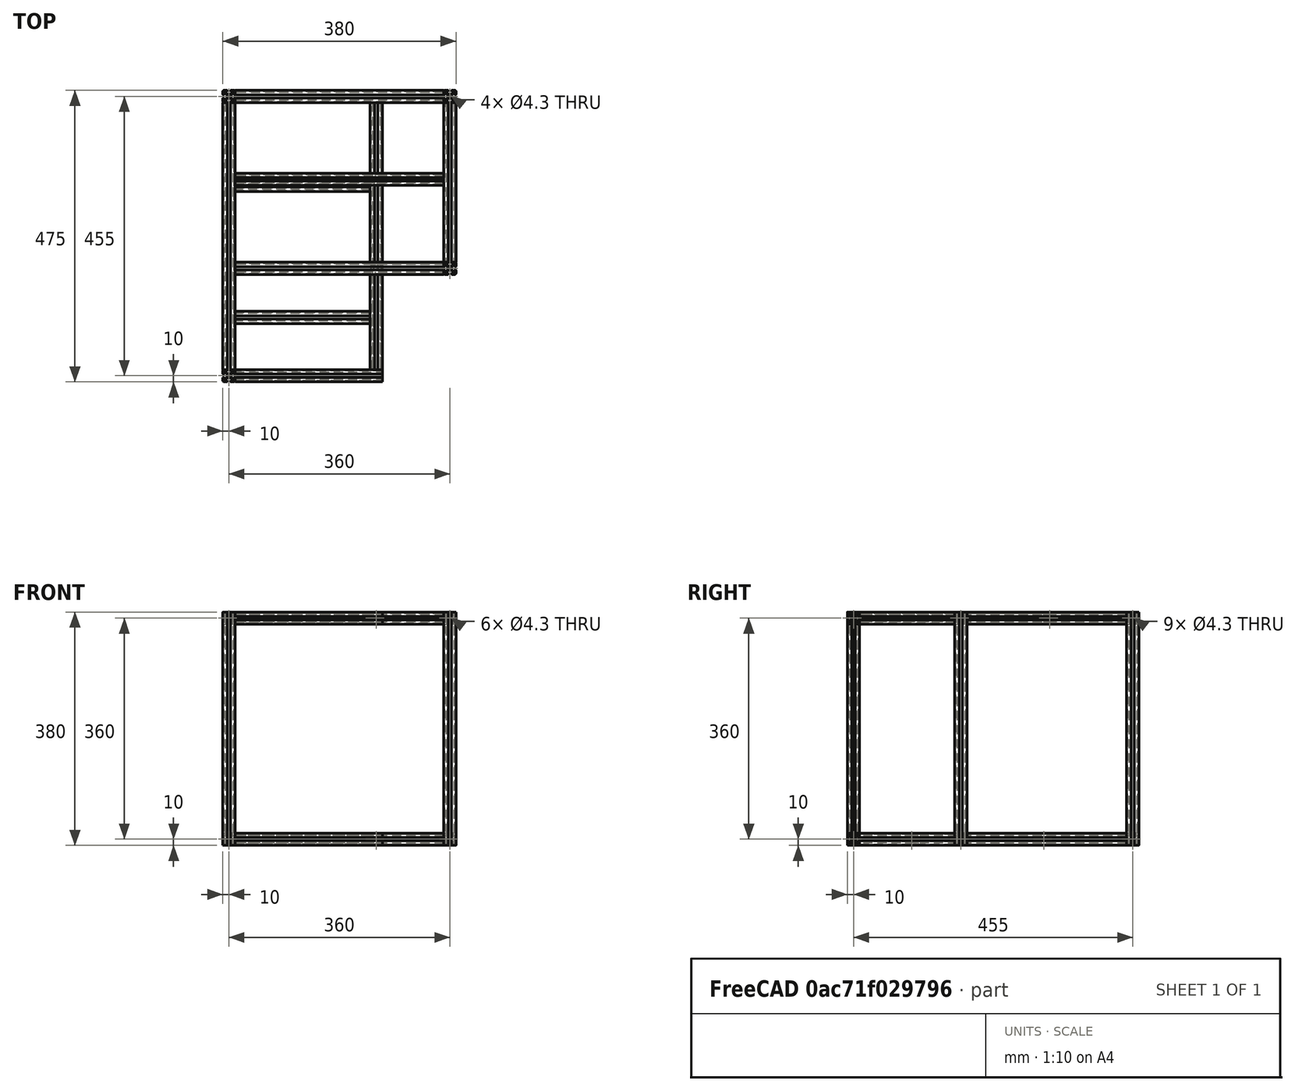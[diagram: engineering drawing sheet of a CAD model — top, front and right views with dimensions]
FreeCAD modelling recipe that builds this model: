
FCSTD DOCUMENT  (FreeCAD 0.18R)
Label: K-MINI-Enclosure-Frame
License: All rights reserved
LicenseURL: http://en.wikipedia.org/wiki/All_rights_reserved
objects: Drawing::FeatureViewPython×22, PartDesign::Pad×19, PartDesign::Body×19, Drawing::FeatureViewPart×4, Part::Compound×3, Drawing::FeaturePage×2, Sketcher::SketchObject×1, App::Part×1
note: 61 computed .brp shape members not serialized (recipe doc carries the construction recipe); baked Part::Feature solids carry a one-line shape summary decoded from their .brp

FEATURE [Sketcher::SketchObject] CopySketch029  label="ISP5-L20-Profile001"
  MapMode = 5
  sketch-geometry (70):
    g0: LineSegment StartX=-2.5 StartY=3.5 StartZ=0 EndX=-5.91967 EndY=6.91967 EndZ=0
    g1: LineSegment StartX=-5.38934 StartY=8.2 StartZ=0 EndX=-2.85 EndY=8.2 EndZ=0
    g2: LineSegment StartX=-3.35 StartY=10 StartZ=0 EndX=-8 EndY=10 EndZ=0
    g3: LineSegment StartX=-10 StartY=8 StartZ=0 EndX=-10 EndY=3.35 EndZ=0
    g4: LineSegment StartX=-9.25 StartY=2.6 StartZ=0 EndX=-8.45 EndY=2.6 EndZ=0
    g5: LineSegment StartX=-8.2 StartY=2.85 StartZ=0 EndX=-8.2 EndY=5.38934 EndZ=0
    g6: LineSegment StartX=-6.91967 StartY=5.91967 StartZ=0 EndX=-3.5 EndY=2.5 EndZ=0
    g7: LineSegment StartX=-2.6 StartY=9.25 StartZ=0 EndX=-2.6 EndY=8.45 EndZ=0
    g8: ArcOfCircle CenterX=-8 CenterY=8 CenterZ=0 NormalX=0 NormalY=0 NormalZ=1 AngleXU=0 Radius=2 StartAngle=1.5708 EndAngle=3.14159
    g9: ArcOfCircle CenterX=-3.35 CenterY=9.25 CenterZ=0 NormalX=0 NormalY=0 NormalZ=1 AngleXU=0 Radius=0.75 StartAngle=6e-16 EndAngle=1.5708
    g10: ArcOfCircle CenterX=-9.25 CenterY=3.35 CenterZ=0 NormalX=0 NormalY=0 NormalZ=1 AngleXU=0 Radius=0.75 StartAngle=3.14159 EndAngle=4.71239
    g11: ArcOfCircle CenterX=-5.38934 CenterY=7.45 CenterZ=0 NormalX=0 NormalY=0 NormalZ=1 AngleXU=0 Radius=0.75 StartAngle=1.5708 EndAngle=3.92699
    g12: ArcOfCircle CenterX=-7.45 CenterY=5.38934 CenterZ=0 NormalX=0 NormalY=0 NormalZ=1 AngleXU=0 Radius=0.75 StartAngle=0.785398 EndAngle=3.14159
    g13: LineSegment [constr] StartX=-5.38934 StartY=7.45 StartZ=0 EndX=-7.45 EndY=5.38934 EndZ=0
    g14: ArcOfCircle CenterX=-2.85 CenterY=8.45 CenterZ=0 NormalX=0 NormalY=0 NormalZ=1 AngleXU=0 Radius=0.25 StartAngle=4.71239 EndAngle=6.28319
    g15: Circle CenterX=0 CenterY=0 CenterZ=0 NormalX=0 NormalY=0 NormalZ=1 AngleXU=0 Radius=2.15
    g16: LineSegment StartX=2.5 StartY=3.5 StartZ=0 EndX=5.91967 EndY=6.91967 EndZ=0
    g17: LineSegment StartX=3.5 StartY=-2.5 StartZ=0 EndX=6.91967 EndY=-5.91967 EndZ=0
    g18: LineSegment StartX=2.5 StartY=-3.5 StartZ=0 EndX=5.91967 EndY=-6.91967 EndZ=0
    g19: LineSegment StartX=-2.5 StartY=-3.5 StartZ=0 EndX=-5.91967 EndY=-6.91967 EndZ=0
    g20: LineSegment StartX=-3.5 StartY=-2.5 StartZ=0 EndX=-6.91967 EndY=-5.91967 EndZ=0
    g21: LineSegment StartX=3.5 StartY=2.5 StartZ=0 EndX=6.91967 EndY=5.91967 EndZ=0
    g22: ArcOfCircle CenterX=-7.45 CenterY=-5.38934 CenterZ=0 NormalX=0 NormalY=0 NormalZ=1 AngleXU=0 Radius=0.75 StartAngle=3.14159 EndAngle=5.49779
    g23: ArcOfCircle CenterX=-5.38934 CenterY=-7.45 CenterZ=0 NormalX=0 NormalY=0 NormalZ=1 AngleXU=0 Radius=0.75 StartAngle=2.35619 EndAngle=4.71239
    g24: ArcOfCircle CenterX=5.38934 CenterY=-7.45 CenterZ=0 NormalX=0 NormalY=0 NormalZ=1 AngleXU=0 Radius=0.75 StartAngle=4.71239 EndAngle=7.06858
    g25: ArcOfCircle CenterX=7.45 CenterY=-5.38934 CenterZ=0 NormalX=0 NormalY=0 NormalZ=1 AngleXU=0 Radius=0.75 StartAngle=3.92699 EndAngle=6.28319
    g26: ArcOfCircle CenterX=5.38934 CenterY=7.45 CenterZ=0 NormalX=0 NormalY=0 NormalZ=1 AngleXU=0 Radius=0.75 StartAngle=5.49779 EndAngle=7.85398
    g27: ArcOfCircle CenterX=7.45 CenterY=5.38934 CenterZ=0 NormalX=0 NormalY=0 NormalZ=1 AngleXU=0 Radius=0.75 StartAngle=6e-16 EndAngle=2.35619
    g28: LineSegment StartX=-5.38934 StartY=-8.2 StartZ=0 EndX=-2.85 EndY=-8.2 EndZ=0
    g29: LineSegment StartX=2.85 StartY=-8.2 StartZ=0 EndX=5.38934 EndY=-8.2 EndZ=0
    g30: LineSegment StartX=8.2 StartY=-5.38934 StartZ=0 EndX=8.2 EndY=-2.85 EndZ=0
    g31: LineSegment StartX=8.2 StartY=5.38934 StartZ=0 EndX=8.2 EndY=2.85 EndZ=0
    g32: LineSegment StartX=5.38934 StartY=8.2 StartZ=0 EndX=2.85 EndY=8.2 EndZ=0
    g33: LineSegment StartX=-8.2 StartY=-5.38934 StartZ=0 EndX=-8.2 EndY=-2.85 EndZ=0
    g34: ArcOfCircle CenterX=-8.45 CenterY=-2.85 CenterZ=0 NormalX=0 NormalY=0 NormalZ=1 AngleXU=0 Radius=0.25 StartAngle=7e-16 EndAngle=1.5708
    g35: ArcOfCircle CenterX=-2.85 CenterY=-8.45 CenterZ=0 NormalX=0 NormalY=0 NormalZ=1 AngleXU=0 Radius=0.25 StartAngle=1e-15 EndAngle=1.5708
    g36: ArcOfCircle CenterX=2.85 CenterY=-8.45 CenterZ=0 NormalX=0 NormalY=0 NormalZ=1 AngleXU=0 Radius=0.25 StartAngle=1.5708 EndAngle=3.14159
    g37: ArcOfCircle CenterX=8.45 CenterY=-2.85 CenterZ=0 NormalX=0 NormalY=0 NormalZ=1 AngleXU=0 Radius=0.25 StartAngle=1.5708 EndAngle=3.14159
    g38: LineSegment StartX=2.6 StartY=9.25 StartZ=0 EndX=2.6 EndY=8.45 EndZ=0
    g39: LineSegment StartX=8.45 StartY=2.6 StartZ=0 EndX=9.25 EndY=2.6 EndZ=0
    g40: LineSegment StartX=8.45 StartY=-2.6 StartZ=0 EndX=9.25 EndY=-2.6 EndZ=0
    g41: LineSegment StartX=-8.45 StartY=-2.6 StartZ=0 EndX=-9.25 EndY=-2.6 EndZ=0
    g42: LineSegment StartX=-2.6 StartY=-8.45 StartZ=0 EndX=-2.6 EndY=-9.25 EndZ=0
    g43: LineSegment StartX=2.6 StartY=-8.45 StartZ=0 EndX=2.6 EndY=-9.25 EndZ=0
    g44: ArcOfCircle CenterX=8.45 CenterY=2.85 CenterZ=0 NormalX=0 NormalY=0 NormalZ=1 AngleXU=0 Radius=0.25 StartAngle=3.14159 EndAngle=4.71239
    g45: LineSegment StartX=3.35 StartY=10 StartZ=0 EndX=8 EndY=10 EndZ=0
    g46: ArcOfCircle CenterX=8 CenterY=8 CenterZ=0 NormalX=0 NormalY=0 NormalZ=1 AngleXU=0 Radius=2 StartAngle=2e-16 EndAngle=1.5708
    g47: LineSegment StartX=10 StartY=8 StartZ=0 EndX=10 EndY=3.35 EndZ=0
    g48: ArcOfCircle CenterX=9.25 CenterY=3.35 CenterZ=0 NormalX=0 NormalY=0 NormalZ=1 AngleXU=0 Radius=0.75 StartAngle=4.71239 EndAngle=6.28319
    g49: LineSegment StartX=3.35 StartY=-10 StartZ=0 EndX=8 EndY=-10 EndZ=0
    g50: ArcOfCircle CenterX=8 CenterY=-8 CenterZ=0 NormalX=0 NormalY=0 NormalZ=1 AngleXU=0 Radius=2 StartAngle=4.71239 EndAngle=6.28319
    g51: LineSegment StartX=10 StartY=-8 StartZ=0 EndX=10 EndY=-3.35 EndZ=0
    g52: ArcOfCircle CenterX=9.25 CenterY=-3.35 CenterZ=0 NormalX=0 NormalY=0 NormalZ=1 AngleXU=0 Radius=0.75 StartAngle=1e-16 EndAngle=1.5708
    g53: LineSegment StartX=-3.35 StartY=-10 StartZ=0 EndX=-8 EndY=-10 EndZ=0
    g54: LineSegment StartX=-10 StartY=-8 StartZ=0 EndX=-10 EndY=-3.35 EndZ=0
    g55: ArcOfCircle CenterX=-9.25 CenterY=-3.35 CenterZ=0 NormalX=0 NormalY=0 NormalZ=1 AngleXU=0 Radius=0.75 StartAngle=1.5708 EndAngle=3.14159
    g56: ArcOfCircle CenterX=-3.35 CenterY=-9.25 CenterZ=0 NormalX=0 NormalY=0 NormalZ=1 AngleXU=0 Radius=0.75 StartAngle=4.71239 EndAngle=6.28319
    g57: ArcOfCircle CenterX=3.35 CenterY=-9.25 CenterZ=0 NormalX=0 NormalY=0 NormalZ=1 AngleXU=0 Radius=0.75 StartAngle=3.14159 EndAngle=4.71239
    g58: ArcOfCircle CenterX=3.35 CenterY=9.25 CenterZ=0 NormalX=0 NormalY=0 NormalZ=1 AngleXU=0 Radius=0.75 StartAngle=1.5708 EndAngle=3.14159
    g59: ArcOfCircle CenterX=-8 CenterY=-8 CenterZ=0 NormalX=0 NormalY=0 NormalZ=1 AngleXU=0 Radius=2 StartAngle=3.14159 EndAngle=4.71239
    g60: ArcOfCircle CenterX=-8.45 CenterY=2.85 CenterZ=0 NormalX=0 NormalY=0 NormalZ=1 AngleXU=0 Radius=0.25 StartAngle=4.71239 EndAngle=6.28319
    g61: ArcOfCircle CenterX=2.85 CenterY=8.45 CenterZ=0 NormalX=0 NormalY=0 NormalZ=1 AngleXU=0 Radius=0.25 StartAngle=3.14159 EndAngle=4.71239
    g62: LineSegment StartX=0 StartY=3.5 StartZ=0 EndX=2.5 EndY=3.5 EndZ=0
    g63: LineSegment StartX=0 StartY=3.5 StartZ=0 EndX=-2.5 EndY=3.5 EndZ=0
    g64: LineSegment StartX=-3.5 StartY=2.5 StartZ=0 EndX=-3.5 EndY=0 EndZ=0
    g65: LineSegment StartX=-3.5 StartY=0 StartZ=0 EndX=-3.5 EndY=-2.5 EndZ=0
    g66: LineSegment StartX=-2.5 StartY=-3.5 StartZ=0 EndX=0 EndY=-3.5 EndZ=0
    g67: LineSegment StartX=0 StartY=-3.5 StartZ=0 EndX=2.5 EndY=-3.5 EndZ=0
    g68: LineSegment StartX=3.5 StartY=-2.5 StartZ=0 EndX=3.5 EndY=0 EndZ=0
    g69: LineSegment StartX=3.5 StartY=0 StartZ=0 EndX=3.5 EndY=2.5 EndZ=0
  constraints (173):
    c: Vertical(g7)
    c: Horizontal(g1)
    c: Vertical(g5)
    c: Horizontal(g4)
    c: Coincident(g2,g9)
    c: Coincident(g9,g7)
    c: Radius(g9) = 0.75
    c: DistanceY(g1,g2) = 1.8
    c: Coincident(g3,g10)
    c: Coincident(g10,g4)
    c: Radius(g10) = 0.75
    c: Horizontal(g9,g7)
    c: Vertical(g2,g9)
    c: Coincident(g0,g11)
    c: Coincident(g11,g1)
    c: Vertical(g1,g11)
    c: Radius(g11) = 0.75
    c: Coincident(g12,g6)
    c: Coincident(g12,g5)
    c: Equal(g11,g12)
    c: Horizontal(g5,g12)
    c: Coincident(g12,g13)
    c: Coincident(g11,g13)
    c: PointOnObject(g0,g13)
    c: PointOnObject(g6,g13)
    c: Horizontal(g3,g10)
    c: Vertical(g10,g4)
    c: Horizontal(g2)
    c: Vertical(g3)
    c: Parallel(g6,g0)
    c: Tangent(g2,g8) = -1.5708
    c: Tangent(g3,g8) = -1.5708
    c: Radius(g8) = 2
    c: Perpendicular(g13,g6)
    c: Coincident(g7,g14)
    c: Coincident(g1,g14)
    c: Vertical(g14,g1)
    c: Horizontal(g14,g7)
    c: Radius(g14) = 0.25
    c: DistanceX(g3,g5) = 1.8
    c: Coincident(g15,g-1)
    c: Radius(g15) = 2.15
    c: DistanceX(g0,g16) = 5
    c: Symmetric(g16,g0,g-2)
    c: Symmetric(g21,g6,g-2)
    c: Equal(g16,g21)
    c: Parallel(g20,g19)
    c: Parallel(g18,g17)
    c: Symmetric(g6,g20,g-1)
    c: Symmetric(g0,g19,g-1)
    c: Tangent(g16,g26) = -1.5708
    c: Tangent(g21,g27) = 1.5708
    c: Tangent(g17,g25) = -1.5708
    c: Tangent(g18,g24) = 1.5708
    c: Tangent(g19,g23) = -1.5708
    c: Tangent(g20,g22) = 1.5708
    c: Horizontal(g28)
    c: Tangent(g26,g32) = -1.5708
    c: Tangent(g27,g31) = 1.5708
    c: Tangent(g25,g30) = -1.5708
    c: Tangent(g24,g29) = -1.5708
    c: Tangent(g23,g28) = -1.5708
    c: Tangent(g22,g33) = 1.5708
    c: Tangent(g30,g37) = 1.5708
    c: Tangent(g36,g29) = 1.5708
    c: Tangent(g28,g35) = 1.5708
    c: Tangent(g34,g33) = -1.5708
    c: Symmetric(g0,g16,g-2)
    c: Symmetric(g21,g17,g-1)
    c: Symmetric(g18,g19,g-2)
    c: Symmetric(g6,g20,g-1)
    c: Symmetric(g23,g1,g-1)
    c: Symmetric(g24,g26,g-1)
    c: DistanceX(g6,g21) = 7
    c: Vertical(g42)
    c: Vertical(g43)
    c: Tangent(g44,g31) = -1.5708
    c: Tangent(g44,g39) = -1.5708
    c: Tangent(g37,g40) = 1.5708
    c: Tangent(g36,g43) = -1.5708
    c: Tangent(g35,g42) = 1.5708
    c: Tangent(g41,g34) = -1.5708
    c: Symmetric(g5,g27,g-2)
    c: Symmetric(g22,g25,g-2)
    c: Vertical(g7,g35)
    c: Symmetric(g4,g41,g-1)
    c: Symmetric(g7,g38,g-2)
    c: Symmetric(g39,g40,g-1)
    c: Tangent(g45,g46) = 1.5708
    c: Tangent(g46,g47) = 1.5708
    c: Tangent(g47,g48) = 1.5708
    c: Tangent(g49,g50) = -1.5708
    c: Tangent(g50,g51) = -1.5708
    c: Tangent(g51,g52) = -1.5708
    c: Tangent(g54,g55) = 1.5708
    c: Tangent(g55,g41) = -1.5708
    c: Tangent(g40,g52) = 1.5708
    c: Tangent(g48,g39) = -1.5708
    c: Vertical(g51)
    c: Vertical(g47)
    c: Horizontal(g45)
    c: Horizontal(g49)
    c: Horizontal(g53)
    c: Tangent(g45,g58) = 1.5708
    c: Tangent(g38,g58) = -1.5708
    c: Tangent(g43,g57) = -1.5708
    c: Tangent(g49,g57) = -1.5708
    c: Tangent(g53,g56) = 1.5708
    c: Tangent(g42,g56) = 1.5708
    c: DistanceX(g3,g46) = 20
    c: Tangent(g54,g59) = 1.5708
    c: Tangent(g53,g59) = 1.5708
    c: DistanceY(g53,g2) = 20
    c: Symmetric(g54,g51,g-2)
    c: Vertical(g51,g47)
    c: Horizontal(g39)
    c: Horizontal(g40)
    c: Vertical(g54)
    c: DistanceX(g7,g38) = 5.2
    c: DistanceY(g41,g4) = 5.2
    c: DistanceY(g40,g39) = 5.2
    c: Horizontal(g2,g45)
    c: Vertical(g3,g54)
    c: Horizontal(g53,g49)
    c: Vertical(g38)
    c: Horizontal(g32)
    c: Vertical(g30)
    c: Vertical(g31)
    c: Vertical(g33)
    c: Vertical(g5,g33)
    c: Horizontal(g41)
    c: Radius(g46) = 2
    c: Radius(g50) = 2
    c: Radius(g59) = 2
    c: Radius(g56) = 0.75
    c: Symmetric(g42,g43,g-2)
    c: Radius(g35) = 0.25
    c: Radius(g44) = 0.25
    c: Radius(g34) = 0.25
    c: Radius(g37) = 0.25
    c: Tangent(g5,g60) = -1.5708
    c: Tangent(g4,g60) = -1.5708
    c: Radius(g60) = 0.25
    c: Tangent(g61,g38) = -1.5708
    c: Tangent(g32,g61) = 1.5708
    c: Radius(g61) = 0.25
    c: Radius(g36) = 0.25
    c: Horizontal(g1,g32)
    c: Coincident(g62,g63)
    c: Horizontal(g63)
    c: PointOnObject(g62,g-2)
    c: Coincident(g16,g62)
    c: Coincident(g0,g63)
    c: Coincident(g68,g69)
    c: Coincident(g66,g67)
    c: Coincident(g64,g65)
    c: Coincident(g20,g65)
    c: Coincident(g19,g66)
    c: Coincident(g18,g67)
    c: Coincident(g17,g68)
    c: Coincident(g21,g69)
    c: Coincident(g6,g64)
    c: PointOnObject(g64,g-1)
    c: PointOnObject(g68,g-1)
    c: PointOnObject(g66,g-2)
    c: Vertical(g64)
    c: Horizontal(g66)
    c: Horizontal(g67)
    c: Vertical(g69)
    c: Vertical(g68)
    c: DistanceY(g20,g6) = 5
    c: DistanceY(g19,g0) = 7
    c: Vertical(g16,g18)
FEATURE [PartDesign::Pad] Pad
  Length = 380
  Length2 = 0
  Profile = -> CopySketch029
  Type = 0
FEATURE [PartDesign::Body] Body003  label="V-Front-Left"
  Group = -> [Pad]
  Origin = -> Origin008
  Placement = pos=(-215,-240,-50) rot=(0,0,1;0rad)
  Tip = -> Pad
FEATURE [PartDesign::Pad] Pad002
  Length = 380
  Length2 = 0
  Profile = -> CopySketch029
  Type = 0
FEATURE [PartDesign::Body] Body004  label="V-Back-Left"
  Group = -> [Pad002]
  Origin = -> Origin009
  Placement = pos=(-215,215,-50) rot=(0,0,1;0rad)
  Tip = -> Pad002
FEATURE [PartDesign::Pad] Pad003
  Length = 100
  Length2 = 0
  Profile = -> CopySketch029
  Type = 0
FEATURE [PartDesign::Body] Body005  label="B-X-Right"
  Group = -> [Pad003]
  Origin = -> Origin010
  Placement = pos=(35,-65,-40) rot=(0,1,0;1.5708rad)
  Tip = -> Pad003
FEATURE [PartDesign::Pad] Pad004
  Length = 380
  Length2 = 0
  Profile = -> CopySketch029
  Type = 0
FEATURE [PartDesign::Body] Body006  label="V-Back-Right"
  Group = -> [Pad004]
  Origin = -> Origin011
  Placement = pos=(145,215,-50) rot=(0,0,1;0rad)
  Tip = -> Pad004
FEATURE [PartDesign::Pad] Pad008
  Length = 220
  Length2 = 0
  Profile = -> CopySketch029
  Type = 0
FEATURE [PartDesign::Body] Body010  label="B-Carrier-Back"
  Group = -> [Pad008]
  Origin = -> Origin015
  Placement = pos=(-205,70,-40) rot=(0,1,0;1.5708rad)
  Tip = -> Pad008
FEATURE [PartDesign::Pad] Pad009
  Length = 340
  Length2 = 0
  Profile = -> CopySketch029
  Type = 0
FEATURE [PartDesign::Body] Body011  label="T-X-Back"
  Group = -> [Pad009]
  Origin = -> Origin016
  Placement = pos=(-205,215,320) rot=(0,1,0;1.5708rad)
  Tip = -> Pad009
FEATURE [PartDesign::Pad] Pad010
  Length = 240
  Length2 = 0
  Profile = -> CopySketch029
  Type = 0
FEATURE [PartDesign::Body] Body012  label="T-X-Front"
  Group = -> [Pad010]
  Origin = -> Origin017
  Placement = pos=(35,-240,320) rot=(0.707107,0,-0.707107;3.14159rad)
  Tip = -> Pad010
FEATURE [PartDesign::Pad] Pad011
  Length = 220
  Length2 = 0
  Profile = -> CopySketch029
  Type = 0
FEATURE [PartDesign::Body] Body013  label="B-Carrier-Front"
  Group = -> [Pad011]
  Origin = -> Origin018
  Placement = pos=(-205,-145,-40) rot=(0,1,0;1.5708rad)
  Tip = -> Pad011
FEATURE [PartDesign::Pad] Pad012
  Length = 435
  Length2 = 0
  Profile = -> CopySketch029
  Type = 0
FEATURE [PartDesign::Body] Body014  label="B-Y-Left"
  Group = -> [Pad012]
  Origin = -> Origin019
  Placement = pos=(-215,-230,-40) rot=(0.57735,-0.57735,-0.57735;4.18879rad)
  Tip = -> Pad012
FEATURE [PartDesign::Pad] Pad013
  Length = 260
  Length2 = 0
  Profile = -> CopySketch029
  Type = 0
FEATURE [PartDesign::Body] Body015  label="B-Y-Right"
  Group = -> [Pad013]
  Origin = -> Origin020
  Placement = pos=(145,-55,-40) rot=(0.57735,-0.57735,-0.57735;4.18879rad)
  Tip = -> Pad013
FEATURE [PartDesign::Pad] Pad014
  Length = 340
  Length2 = 0
  Profile = -> CopySketch029
  Type = 0
FEATURE [PartDesign::Body] Body016  label="T-X-Middle"
  Group = -> [Pad014]
  Origin = -> Origin021
  Placement = pos=(-205,-65,320) rot=(0,1,0;1.5708rad)
  Tip = -> Pad014
FEATURE [PartDesign::Pad] Pad015
  Length = 435
  Length2 = 0
  Profile = -> CopySketch029
  Type = 0
FEATURE [PartDesign::Body] Body017  label="T-Y-Left"
  Group = -> [Pad015]
  Origin = -> Origin022
  Placement = pos=(-215,-230,320) rot=(0.57735,-0.57735,-0.57735;4.18879rad)
  Tip = -> Pad015
FEATURE [PartDesign::Pad] Pad016
  Length = 240
  Length2 = 0
  Profile = -> CopySketch029
  Type = 0
FEATURE [PartDesign::Body] Body019  label="B-X-Front"
  Group = -> [Pad016]
  Origin = -> Origin024
  Placement = pos=(35,-240,-40) rot=(0.707107,0,-0.707107;3.14159rad)
  Tip = -> Pad016
FEATURE [PartDesign::Pad] Pad017
  Length = 340
  Length2 = 0
  Profile = -> CopySketch029
  Type = 0
FEATURE [PartDesign::Body] Body020  label="B-X-Back"
  Group = -> [Pad017]
  Origin = -> Origin025
  Placement = pos=(-205,215,-40) rot=(0,1,0;1.5708rad)
  Tip = -> Pad017
FEATURE [PartDesign::Pad] Pad018
  Length = 380
  Length2 = 0
  Profile = -> CopySketch029
  Type = 0
FEATURE [PartDesign::Body] Body021  label="V-Front-Right"
  Group = -> [Pad018]
  Origin = -> Origin026
  Placement = pos=(145,-65,-50) rot=(0,0,1;0rad)
  Tip = -> Pad018
FEATURE [Part::Compound] Compound  label="Vertical"
  Links = -> [Body003,Body004,Body006,Body021]
FEATURE [PartDesign::Pad] Pad019
  Length = 260
  Length2 = 0
  Profile = -> CopySketch029
  Type = 0
FEATURE [PartDesign::Body] Body022  label="T-Y-Right"
  Group = -> [Pad019]
  Origin = -> Origin027
  Placement = pos=(145,-55,320) rot=(0.57735,-0.57735,-0.57735;4.18879rad)
  Tip = -> Pad019
FEATURE [PartDesign::Pad] Pad024
  Length = 435
  Length2 = 0
  Profile = -> CopySketch029
  Type = 0
FEATURE [PartDesign::Body] Body027  label="B-Y-Mid"
  Group = -> [CopySketch029,Pad024]
  Origin = -> Origin032
  Placement = pos=(25,-230,-40) rot=(-1,0,0;1.5708rad)
  Tip = -> Pad024
FEATURE [Part::Compound] Compound001  label="Bottom"
  Links = -> [Body013,Body010,Body014,Body015,Body019,Body020,Body027,Body005]
FEATURE [PartDesign::Pad] Pad025
  Length = 155
  Length2 = 0
  Profile = -> CopySketch029
  Type = 0
FEATURE [PartDesign::Body] Body028  label="T-Y-Mid"
  Group = -> [Pad025]
  Origin = -> Origin033
  Placement = pos=(25,-230,320) rot=(-1,0,0;1.5708rad)
  Tip = -> Pad025
FEATURE [PartDesign::Pad] Pad026
  Length = 340
  Length2 = 100
  Profile = -> CopySketch029
  Type = 0
FEATURE [PartDesign::Body] Body029  label="T-X-HandleRear"
  Group = -> [Pad026]
  Origin = -> Origin034
  Placement = pos=(-205,80,320) rot=(0,1,0;1.5708rad)
  Tip = -> Pad026
FEATURE [Part::Compound] Compound002  label="Top"
  Links = -> [Body011,Body012,Body016,Body017,Body022,Body028,Body029]
FEATURE [App::Part] Part002  label="K-MINI-Enclosure-Frame"
  Group = -> [Body003,Body004,Body005,Body006,Compound,Body010,Body013,Compound001,Body011,Body012,Body016,Body017,Compound002]
  Origin = -> Origin004
FEATURE [Drawing::FeatureViewPart] View
  Direction = (0,0,1)
  HiddenWidth = 0.15
  LineWidth = 0.35
  Rotation = 0
  Scale = 0.25
  ShowHiddenLines = false
  ShowSmoothLines = false
  Source = -> Compound
  Tolerance = 0.05
  ViewResult = <blob: 15307 chars omitted>
  Visible = false
  X = 113.75
  Y = 145.375
FEATURE [Drawing::FeatureViewPart] View001
  Direction = (0,0,1)
  HiddenWidth = 0.15
  LineWidth = 0.35
  Rotation = 0
  Scale = 0.25
  ShowHiddenLines = false
  ShowSmoothLines = false
  Source = -> Compound002
  Tolerance = 0.05
  ViewResult = <blob: 27314 chars omitted>
  Visible = false
  X = 113.75
  Y = 145.375
FEATURE [Drawing::FeatureViewPython] centerLines001  # drawing view (typed FeaturePython)
  Rotation = 0
  ViewResult = <g transform="scale(0.250000,0.250000)" stroke="rgb(0,0,255)"  stroke-width="1.280000" > <path d="M 250.000000,646.500000 L 244.000000,646.500000 M 236.000000,646.500000 L 219.817495,646.500000 "/>\n<path d="M 250.000000,646.500000 L 244.000000,646.500000 M 236.000000,646.500000 L 219.817495,646.500000 "/> </g> 
  Visible = false
  X = 0
  Y = 0
  centerLine_color = rgb(0,0,255)
  centerLine_len_dash = 6
  centerLine_len_dot = 1.5
  centerLine_len_gap = 2
  centerLine_width = 0.32
  click1_x = 54.9544
  click1_y = 162.545
  click2_x = 54.9544
  click2_y = 161.848
FEATURE [Drawing::FeatureViewPython] centerLines002  # drawing view (typed FeaturePython)
  Rotation = 0
  ViewResult = <g transform="scale(0.250000,0.250000)" stroke="rgb(0,0,255)"  stroke-width="1.280000" > <path d="M 250.000000,501.500000 L 244.000000,501.500000 M 236.000000,501.500000 L 221.485575,501.500000 "/>\n<path d="M 250.000000,501.500000 L 244.000000,501.500000 M 236.000000,501.500000 L 218.300495,501.500000 "/> </g> 
  Visible = false
  X = 0
  Y = 0
  centerLine_color = rgb(0,0,255)
  centerLine_len_dash = 6
  centerLine_len_dot = 1.5
  centerLine_len_gap = 2
  centerLine_width = 0.32
  click1_x = 55.3714
  click1_y = 125.259
  click2_x = 54.5751
  click2_y = 123.912
FEATURE [Drawing::FeatureViewPython] dim001  # drawing view (typed FeaturePython)
  Rotation = 0
  ViewResult = <g> \n  <line x1="55.888750" y1="202.875000" x2="44.894828" y2="202.875000" style="stroke:rgb(0,0,255);stroke-width:0.50" />\n<line x1="52.954374" y1="161.625000" x2="44.894828" y2="161.625000" style="stroke:rgb(0,0,255);stroke-width:0.50" />\n<line x1="45.894828" y1="202.875000" x2="45.894828" y2="161.625000" style="stroke:rgb(0,0,255);stroke-width:0.50" /> \n  <polygon points="45.894828,161.625000 44.894828,164.625000 45.894828,165.625000 46.894828,164.625000" style="fill:rgb(0,0,255);stroke:rgb(0,0,255);stroke-width:0" /><polygon points="45.894828,202.875000 46.894828,199.875000 45.894828,198.875000 44.894828,199.875000" style="fill:rgb(0,0,255);stroke:rgb(0,0,255);stroke-width:0" /> \n  <text x="43.894828" y="182.250000" font-family="inherit" font-size="3.6" fill="rgb(0,0,255)" text-anchor="middle" transform="rotate(-90.000000 43.894828,182.250000)" >165</text> </g>
  Visible = false
  X = 0
  Y = 0
  arrowL1 = 3
  arrowL2 = 1
  arrowW = 2
  arrow_scheme = 0
  autoPlaceOffset = 2
  autoPlaceText = true
  click1_x = 45.8948
  click1_y = 175.463
  click2_x = 45.8948
  click2_y = 175.463
  comma_decimal_place = false
  dimension_line_overshoot = 1
  gap_datum_points = 2
  halfDimension_linear = false
  lineColor = rgb(0,0,255)
  strokeWidth = 0.5
  textFormat_linear = %(value)3.3f
  textRenderer_color = rgb(0,0,255)
  textRenderer_family = inherit
  textRenderer_size = 3.6
  unit_custom_scale = 1
  unit_scheme = 0
FEATURE [Drawing::FeatureViewPython] dim002  # drawing view (typed FeaturePython)
  Rotation = 0
  ViewResult = <g> \n  <line x1="55.888750" y1="94.125000" x2="44.156754" y2="94.125000" style="stroke:rgb(0,0,255);stroke-width:0.50" />\n<line x1="53.371394" y1="125.375000" x2="44.156754" y2="125.375000" style="stroke:rgb(0,0,255);stroke-width:0.50" />\n<line x1="45.156754" y1="94.125000" x2="45.156754" y2="125.375000" style="stroke:rgb(0,0,255);stroke-width:0.50" /> \n  <polygon points="45.156754,125.375000 46.156754,122.375000 45.156754,121.375000 44.156754,122.375000" style="fill:rgb(0,0,255);stroke:rgb(0,0,255);stroke-width:0" /><polygon points="45.156754,94.125000 44.156754,97.125000 45.156754,98.125000 46.156754,97.125000" style="fill:rgb(0,0,255);stroke:rgb(0,0,255);stroke-width:0" /> \n  <text x="43.156754" y="109.750000" font-family="inherit" font-size="3.6" fill="rgb(0,0,255)" text-anchor="middle" transform="rotate(-90.000000 43.156754,109.750000)" >125</text> </g>
  Visible = false
  X = 0
  Y = 0
  arrowL1 = 3
  arrowL2 = 1
  arrowW = 2
  arrow_scheme = 0
  autoPlaceOffset = 2
  autoPlaceText = true
  click1_x = 45.1568
  click1_y = 123.527
  click2_x = 45.1568
  click2_y = 123.527
  comma_decimal_place = false
  dimension_line_overshoot = 1
  gap_datum_points = 2
  halfDimension_linear = false
  lineColor = rgb(0,0,255)
  strokeWidth = 0.5
  textFormat_linear = %(value)3.3f
  textRenderer_color = rgb(0,0,255)
  textRenderer_family = inherit
  textRenderer_size = 3.6
  unit_custom_scale = 1
  unit_scheme = 0
FEATURE [Drawing::FeatureViewPython] centerLines003  # drawing view (typed FeaturePython)
  Rotation = 0
  ViewResult = <g transform="scale(0.250000,0.250000)" stroke="rgb(0,0,255)"  stroke-width="1.280000" > <path d="M 480.000000,656.500000 L 480.000000,650.500000 M 480.000000,642.500000 L 480.000000,619.607087 "/>\n<path d="M 480.000000,656.500000 L 480.000000,650.500000 M 480.000000,642.500000 L 480.000000,619.094261 "/> </g> 
  Visible = false
  X = 0
  Y = 0
  centerLine_color = rgb(0,0,255)
  centerLine_len_dash = 6
  centerLine_len_dot = 1.5
  centerLine_len_gap = 2
  centerLine_width = 0.32
  click1_x = 120.827
  click1_y = 154.902
  click2_x = 120.172
  click2_y = 154.774
FEATURE [Drawing::FeatureViewPython] dim003  # drawing view (typed FeaturePython)
  Rotation = 0
  ViewResult = <g> \n  <line x1="147.500000" y1="157.513750" x2="147.500000" y2="154.324568" style="stroke:rgb(0,0,255);stroke-width:0.50" />\n<line x1="120.000000" y1="156.773565" x2="120.000000" y2="156.324568" style="stroke:rgb(0,0,255);stroke-width:0.50" />\n<line x1="147.500000" y1="155.324568" x2="120.000000" y2="155.324568" style="stroke:rgb(0,0,255);stroke-width:0.50" /> \n  <polygon points="120.000000,155.324568 123.000000,156.324568 124.000000,155.324568 123.000000,154.324568" style="fill:rgb(0,0,255);stroke:rgb(0,0,255);stroke-width:0" /><polygon points="147.500000,155.324568 144.500000,154.324568 143.500000,155.324568 144.500000,156.324568" style="fill:rgb(0,0,255);stroke:rgb(0,0,255);stroke-width:0" /> \n  <text x="133.750000" y="153.324568" font-family="inherit" font-size="3.6" fill="rgb(0,0,255)" text-anchor="middle" transform="rotate(0.000000 133.750000,153.324568)" >110</text> </g>
  Visible = false
  X = 0
  Y = 0
  arrowL1 = 3
  arrowL2 = 1
  arrowW = 2
  arrow_scheme = 0
  autoPlaceOffset = 2
  autoPlaceText = true
  click1_x = 123.718
  click1_y = 155.325
  click2_x = 123.718
  click2_y = 155.325
  comma_decimal_place = false
  dimension_line_overshoot = 1
  gap_datum_points = 2
  halfDimension_linear = false
  lineColor = rgb(0,0,255)
  strokeWidth = 0.5
  textFormat_linear = %(value)3.3f
  textRenderer_color = rgb(0,0,255)
  textRenderer_family = inherit
  textRenderer_size = 3.6
  unit_custom_scale = 1
  unit_scheme = 0
FEATURE [Drawing::FeatureViewPython] dim004  # drawing view (typed FeaturePython)
  Rotation = 0
  ViewResult = <g> \n  <line x1="154.496750" y1="159.125000" x2="180.318263" y2="159.125000" style="stroke:rgb(0,0,255);stroke-width:0.50" />\n<line x1="154.496750" y1="94.125000" x2="180.318263" y2="94.125000" style="stroke:rgb(0,0,255);stroke-width:0.50" />\n<line x1="179.318263" y1="159.125000" x2="179.318263" y2="94.125000" style="stroke:rgb(0,0,255);stroke-width:0.50" /> \n  <polygon points="179.318263,94.125000 178.318263,97.125000 179.318263,98.125000 180.318263,97.125000" style="fill:rgb(0,0,255);stroke:rgb(0,0,255);stroke-width:0" /><polygon points="179.318263,159.125000 180.318263,156.125000 179.318263,155.125000 178.318263,156.125000" style="fill:rgb(0,0,255);stroke:rgb(0,0,255);stroke-width:0" /> \n  <text x="177.318263" y="126.625000" font-family="inherit" font-size="3.6" fill="rgb(0,0,255)" text-anchor="middle" transform="rotate(-90.000000 177.318263,126.625000)" >260</text> </g>
  Visible = false
  X = 0
  Y = 0
  arrowL1 = 3
  arrowL2 = 1
  arrowW = 2
  arrow_scheme = 0
  autoPlaceOffset = 2
  autoPlaceText = true
  click1_x = 179.318
  click1_y = 137.329
  click2_x = 179.318
  click2_y = 137.329
  comma_decimal_place = false
  dimension_line_overshoot = 1
  gap_datum_points = 2
  halfDimension_linear = false
  lineColor = rgb(0,0,255)
  strokeWidth = 0.5
  textFormat_linear = %(value)3.3f
  textRenderer_color = rgb(0,0,255)
  textRenderer_family = inherit
  textRenderer_size = 3.6
  unit_custom_scale = 1
  unit_scheme = 0
FEATURE [Drawing::FeatureViewPython] dim005  # drawing view (typed FeaturePython)
  Rotation = 0
  ViewResult = <g> \n  <line x1="62.500000" y1="87.513750" x2="62.500000" y2="70.400560" style="stroke:rgb(0,0,255);stroke-width:0.50" />\n<line x1="147.500000" y1="87.513750" x2="147.500000" y2="70.400560" style="stroke:rgb(0,0,255);stroke-width:0.50" />\n<line x1="62.500000" y1="71.400560" x2="147.500000" y2="71.400560" style="stroke:rgb(0,0,255);stroke-width:0.50" /> \n  <polygon points="147.500000,71.400560 144.500000,70.400560 143.500000,71.400560 144.500000,72.400560" style="fill:rgb(0,0,255);stroke:rgb(0,0,255);stroke-width:0" /><polygon points="62.500000,71.400560 65.500000,72.400560 66.500000,71.400560 65.500000,70.400560" style="fill:rgb(0,0,255);stroke:rgb(0,0,255);stroke-width:0" /> \n  <text x="105.000000" y="69.400560" font-family="inherit" font-size="3.6" fill="rgb(0,0,255)" text-anchor="middle" transform="rotate(0.000000 105.000000,69.400560)" >340</text> </g>
  Visible = false
  X = 0
  Y = 0
  arrowL1 = 3
  arrowL2 = 1
  arrowW = 2
  arrow_scheme = 0
  autoPlaceOffset = 2
  autoPlaceText = true
  click1_x = 142.402
  click1_y = 71.4006
  click2_x = 142.402
  click2_y = 71.4006
  comma_decimal_place = false
  dimension_line_overshoot = 1
  gap_datum_points = 2
  halfDimension_linear = false
  lineColor = rgb(0,0,255)
  strokeWidth = 0.5
  textFormat_linear = %(value)3.3f
  textRenderer_color = rgb(0,0,255)
  textRenderer_family = inherit
  textRenderer_size = 3.6
  unit_custom_scale = 1
  unit_scheme = 0
FEATURE [Drawing::FeatureViewPython] dim006  # drawing view (typed FeaturePython)
  Rotation = 0
  ViewResult = <g> \n  <line x1="62.500000" y1="209.486250" x2="62.500000" y2="222.108728" style="stroke:rgb(0,0,255);stroke-width:0.50" />\n<line x1="122.500000" y1="209.375000" x2="122.500000" y2="222.108728" style="stroke:rgb(0,0,255);stroke-width:0.50" />\n<line x1="62.500000" y1="221.108728" x2="122.500000" y2="221.108728" style="stroke:rgb(0,0,255);stroke-width:0.50" /> \n  <polygon points="122.500000,221.108728 119.500000,220.108728 118.500000,221.108728 119.500000,222.108728" style="fill:rgb(0,0,255);stroke:rgb(0,0,255);stroke-width:0" /><polygon points="62.500000,221.108728 65.500000,222.108728 66.500000,221.108728 65.500000,220.108728" style="fill:rgb(0,0,255);stroke:rgb(0,0,255);stroke-width:0" /> \n  <text x="92.500000" y="219.108728" font-family="inherit" font-size="3.6" fill="rgb(0,0,255)" text-anchor="middle" transform="rotate(0.000000 92.500000,219.108728)" >240</text> </g>
  Visible = false
  X = 0
  Y = 0
  arrowL1 = 3
  arrowL2 = 1
  arrowW = 2
  arrow_scheme = 0
  autoPlaceOffset = 2
  autoPlaceText = true
  click1_x = 120.582
  click1_y = 221.109
  click2_x = 120.582
  click2_y = 221.109
  comma_decimal_place = false
  dimension_line_overshoot = 1
  gap_datum_points = 2
  halfDimension_linear = false
  lineColor = rgb(0,0,255)
  strokeWidth = 0.5
  textFormat_linear = %(value)3.3f
  textRenderer_color = rgb(0,0,255)
  textRenderer_family = inherit
  textRenderer_size = 3.6
  unit_custom_scale = 1
  unit_scheme = 0
FEATURE [Drawing::FeatureViewPython] dim007  # drawing view (typed FeaturePython)
  Rotation = 0
  ViewResult = <g> \n  <line x1="124.496850" y1="202.875000" x2="135.158546" y2="202.875000" style="stroke:rgb(0,0,255);stroke-width:0.50" />\n<line x1="124.496850" y1="164.125000" x2="135.158546" y2="164.125000" style="stroke:rgb(0,0,255);stroke-width:0.50" />\n<line x1="134.158546" y1="202.875000" x2="134.158546" y2="164.125000" style="stroke:rgb(0,0,255);stroke-width:0.50" /> \n  <polygon points="134.158546,164.125000 133.158546,167.125000 134.158546,168.125000 135.158546,167.125000" style="fill:rgb(0,0,255);stroke:rgb(0,0,255);stroke-width:0" /><polygon points="134.158546,202.875000 135.158546,199.875000 134.158546,198.875000 133.158546,199.875000" style="fill:rgb(0,0,255);stroke:rgb(0,0,255);stroke-width:0" /> \n  <text x="132.158546" y="183.500000" font-family="inherit" font-size="3.6" fill="rgb(0,0,255)" text-anchor="middle" transform="rotate(-90.000000 132.158546,183.500000)" >155</text> </g>
  Visible = false
  X = 0
  Y = 0
  arrowL1 = 3
  arrowL2 = 1
  arrowW = 2
  arrow_scheme = 0
  autoPlaceOffset = 2
  autoPlaceText = true
  click1_x = 134.159
  click1_y = 176.953
  click2_x = 134.159
  click2_y = 176.953
  comma_decimal_place = false
  dimension_line_overshoot = 1
  gap_datum_points = 2
  halfDimension_linear = false
  lineColor = rgb(0,0,255)
  strokeWidth = 0.5
  textFormat_linear = %(value)3.3f
  textRenderer_color = rgb(0,0,255)
  textRenderer_family = inherit
  textRenderer_size = 3.6
  unit_custom_scale = 1
  unit_scheme = 0
FEATURE [Drawing::FeatureViewPython] dim008  # drawing view (typed FeaturePython)
  Rotation = 0
  ViewResult = <g> \n  <line x1="55.783000" y1="94.125000" x2="28.645276" y2="94.125000" style="stroke:rgb(0,0,255);stroke-width:0.50" />\n<line x1="55.888750" y1="202.875000" x2="28.645276" y2="202.875000" style="stroke:rgb(0,0,255);stroke-width:0.50" />\n<line x1="29.645276" y1="94.125000" x2="29.645276" y2="202.875000" style="stroke:rgb(0,0,255);stroke-width:0.50" /> \n  <polygon points="29.645276,202.875000 30.645276,199.875000 29.645276,198.875000 28.645276,199.875000" style="fill:rgb(0,0,255);stroke:rgb(0,0,255);stroke-width:0" /><polygon points="29.645276,94.125000 28.645276,97.125000 29.645276,98.125000 30.645276,97.125000" style="fill:rgb(0,0,255);stroke:rgb(0,0,255);stroke-width:0" /> \n  <text x="27.645276" y="148.500000" font-family="inherit" font-size="3.6" fill="rgb(0,0,255)" text-anchor="middle" transform="rotate(-90.000000 27.645276,148.500000)" >435</text> </g>
  Visible = false
  X = 0
  Y = 0
  arrowL1 = 3
  arrowL2 = 1
  arrowW = 2
  arrow_scheme = 0
  autoPlaceOffset = 2
  autoPlaceText = true
  click1_x = 29.6453
  click1_y = 197.562
  click2_x = 29.6453
  click2_y = 197.562
  comma_decimal_place = false
  dimension_line_overshoot = 1
  gap_datum_points = 2
  halfDimension_linear = false
  lineColor = rgb(0,0,255)
  strokeWidth = 0.5
  textFormat_linear = %(value)3.3f
  textRenderer_color = rgb(0,0,255)
  textRenderer_family = inherit
  textRenderer_size = 3.6
  unit_custom_scale = 1
  unit_scheme = 0
FEATURE [Drawing::FeaturePage] Page  label="TopView"
  Group = -> [View,View001,centerLines001,centerLines002,dim001,dim002,centerLines003,dim003,dim004,dim005,dim006,dim007,dim008]
  Template = <path>
FEATURE [Drawing::FeatureViewPart] View002
  Direction = (0,0,1)
  HiddenWidth = 0.15
  LineWidth = 0.35
  Rotation = 0
  Scale = 0.25
  ShowHiddenLines = false
  ShowSmoothLines = false
  Source = -> Compound
  Tolerance = 0.05
  ViewResult = <blob: 15310 chars omitted>
  Visible = false
  X = 113.75
  Y = 145.375
FEATURE [Drawing::FeatureViewPart] View003
  Direction = (0,0,1)
  HiddenWidth = 0.15
  LineWidth = 0.35
  Rotation = 0
  Scale = 0.25
  ShowHiddenLines = false
  ShowSmoothLines = false
  Source = -> Compound001
  Tolerance = 0.05
  ViewResult = <blob: 30852 chars omitted>
  Visible = false
  X = 113.75
  Y = 145.375
FEATURE [Drawing::FeatureViewPython] centerLines004  # drawing view (typed FeaturePython)
  Rotation = 0
  ViewResult = <g transform="scale(0.250000,0.250000)" stroke="rgb(0,0,255)"  stroke-width="1.280000" > <path d="M 470.000000,511.500000 L 464.000000,511.500000 M 456.000000,511.500000 L 432.000000,511.500000 M 424.000000,511.500000 L 418.000000,511.500000 M 410.000000,511.500000 L 386.000000,511.500000 M 378.000000,511.500000 L 372.000000,511.500000 M 364.000000,511.500000 L 340.000000,511.500000 M 332.000000,511.500000 L 326.000000,511.500000 M 318.000000,511.500000 L 294.000000,511.500000 M 286.000000,511.500000 L 280.000000,511.500000 M 272.000000,511.500000 L 248.000000,511.500000 M 240.000000,511.500000 L 234.000000,511.500000 M 226.000000,511.500000 L 214.991168,511.500000 "/>\n<path d="M 470.000000,511.500000 L 464.000000,511.500000 M 456.000000,511.500000 L 432.000000,511.500000 M 424.000000,511.500000 L 418.000000,511.500000 M 410.000000,511.500000 L 386.000000,511.500000 M 378.000000,511.500000 L 372.000000,511.500000 M 364.000000,511.500000 L 340.000000,511.500000 M 332.000000,511.500000 L 326.000000,511.500000 M 318.000000,511.500000 L 294.000000,511.500000 M 286.000000,511.500000 L 280.000000,511.500000 M 272.000000,511.500000 L 248.000000,511.500000 M 240.000000,511.500000 L 234.000000,511.500000 M 226.000000,511.500000 L 214.991168,511.500000 "/> </g> 
  Visible = false
  X = 0
  Y = 0
  centerLine_color = rgb(0,0,255)
  centerLine_len_dash = 6
  centerLine_len_dot = 1.5
  centerLine_len_gap = 2
  centerLine_width = 0.32
  click1_x = 53.7478
  click1_y = 127.745
  click2_x = 53.7478
  click2_y = 127.745
FEATURE [Drawing::FeatureViewPython] centerLines005  # drawing view (typed FeaturePython)
  Rotation = 0
  ViewResult = <g transform="scale(0.250000,0.250000)" stroke="rgb(0,0,255)"  stroke-width="1.280000" > <path d="M 470.000000,726.500000 L 464.000000,726.500000 M 456.000000,726.500000 L 432.000000,726.500000 M 424.000000,726.500000 L 418.000000,726.500000 M 410.000000,726.500000 L 386.000000,726.500000 M 378.000000,726.500000 L 372.000000,726.500000 M 364.000000,726.500000 L 340.000000,726.500000 M 332.000000,726.500000 L 326.000000,726.500000 M 318.000000,726.500000 L 294.000000,726.500000 M 286.000000,726.500000 L 280.000000,726.500000 M 272.000000,726.500000 L 248.000000,726.500000 M 240.000000,726.500000 L 234.000000,726.500000 M 226.000000,726.500000 L 217.030260,726.500000 "/>\n<path d="M 470.000000,726.500000 L 464.000000,726.500000 M 456.000000,726.500000 L 432.000000,726.500000 M 424.000000,726.500000 L 418.000000,726.500000 M 410.000000,726.500000 L 386.000000,726.500000 M 378.000000,726.500000 L 372.000000,726.500000 M 364.000000,726.500000 L 340.000000,726.500000 M 332.000000,726.500000 L 326.000000,726.500000 M 318.000000,726.500000 L 294.000000,726.500000 M 286.000000,726.500000 L 280.000000,726.500000 M 272.000000,726.500000 L 248.000000,726.500000 M 240.000000,726.500000 L 234.000000,726.500000 M 226.000000,726.500000 L 217.030260,726.500000 "/> </g> 
  Visible = false
  X = 0
  Y = 0
  centerLine_color = rgb(0,0,255)
  centerLine_len_dash = 6
  centerLine_len_dot = 1.5
  centerLine_len_gap = 2
  centerLine_width = 0.32
  click1_x = 54.2576
  click1_y = 179.891
  click2_x = 54.2576
  click2_y = 179.891
FEATURE [Drawing::FeatureViewPython] dim009  # drawing view (typed FeaturePython)
  Rotation = 0
  ViewResult = <g> \n  <line x1="55.888750" y1="202.875000" x2="42.765835" y2="202.875000" style="stroke:rgb(0,0,255);stroke-width:0.50" />\n<line x1="52.257565" y1="181.625000" x2="42.765835" y2="181.625000" style="stroke:rgb(0,0,255);stroke-width:0.50" />\n<line x1="43.765835" y1="202.875000" x2="43.765835" y2="181.625000" style="stroke:rgb(0,0,255);stroke-width:0.50" /> \n  <polygon points="43.765835,181.625000 42.765835,184.625000 43.765835,185.625000 44.765835,184.625000" style="fill:rgb(0,0,255);stroke:rgb(0,0,255);stroke-width:0" /><polygon points="43.765835,202.875000 44.765835,199.875000 43.765835,198.875000 42.765835,199.875000" style="fill:rgb(0,0,255);stroke:rgb(0,0,255);stroke-width:0" /> \n  <text x="41.765835" y="192.250000" font-family="inherit" font-size="3.6" fill="rgb(0,0,255)" text-anchor="middle" transform="rotate(-90.000000 41.765835,192.250000)" >85</text> </g>
  Visible = false
  X = 0
  Y = 0
  arrowL1 = 3
  arrowL2 = 1
  arrowW = 2
  arrow_scheme = 0
  autoPlaceOffset = 2
  autoPlaceText = true
  click1_x = 43.7658
  click1_y = 181.748
  click2_x = 43.7658
  click2_y = 181.748
  comma_decimal_place = false
  dimension_line_overshoot = 1
  gap_datum_points = 2
  halfDimension_linear = false
  lineColor = rgb(0,0,255)
  strokeWidth = 0.5
  textFormat_linear = %(value)3.3f
  textRenderer_color = rgb(0,0,255)
  textRenderer_family = inherit
  textRenderer_size = 3.6
  unit_custom_scale = 1
  unit_scheme = 0
FEATURE [Drawing::FeatureViewPython] dim010  # drawing view (typed FeaturePython)
  Rotation = 0
  ViewResult = <g> \n  <line x1="55.783000" y1="94.125000" x2="47.559392" y2="94.125000" style="stroke:rgb(0,0,255);stroke-width:0.50" />\n<line x1="51.747792" y1="127.875000" x2="47.559392" y2="127.875000" style="stroke:rgb(0,0,255);stroke-width:0.50" />\n<line x1="48.559392" y1="94.125000" x2="48.559392" y2="127.875000" style="stroke:rgb(0,0,255);stroke-width:0.50" /> \n  <polygon points="48.559392,127.875000 49.559392,124.875000 48.559392,123.875000 47.559392,124.875000" style="fill:rgb(0,0,255);stroke:rgb(0,0,255);stroke-width:0" /><polygon points="48.559392,94.125000 47.559392,97.125000 48.559392,98.125000 49.559392,97.125000" style="fill:rgb(0,0,255);stroke:rgb(0,0,255);stroke-width:0" /> \n  <text x="46.559392" y="111.000000" font-family="inherit" font-size="3.6" fill="rgb(0,0,255)" text-anchor="middle" transform="rotate(-90.000000 46.559392,111.000000)" >135</text> </g>
  Visible = false
  X = 0
  Y = 0
  arrowL1 = 3
  arrowL2 = 1
  arrowW = 2
  arrow_scheme = 0
  autoPlaceOffset = 2
  autoPlaceText = true
  click1_x = 48.5594
  click1_y = 122.96
  click2_x = 48.5594
  click2_y = 122.96
  comma_decimal_place = false
  dimension_line_overshoot = 1
  gap_datum_points = 2
  halfDimension_linear = false
  lineColor = rgb(0,0,255)
  strokeWidth = 0.5
  textFormat_linear = %(value)3.3f
  textRenderer_color = rgb(0,0,255)
  textRenderer_family = inherit
  textRenderer_size = 3.6
  unit_custom_scale = 1
  unit_scheme = 0
FEATURE [Drawing::FeatureViewPython] dim011  # drawing view (typed FeaturePython)
  Rotation = 0
  ViewResult = <g> \n  <line x1="55.888750" y1="94.125000" x2="33.890226" y2="94.125000" style="stroke:rgb(0,0,255);stroke-width:0.50" />\n<line x1="55.646500" y1="202.875000" x2="33.890226" y2="202.875000" style="stroke:rgb(0,0,255);stroke-width:0.50" />\n<line x1="34.890226" y1="94.125000" x2="34.890226" y2="202.875000" style="stroke:rgb(0,0,255);stroke-width:0.50" /> \n  <polygon points="34.890226,202.875000 35.890226,199.875000 34.890226,198.875000 33.890226,199.875000" style="fill:rgb(0,0,255);stroke:rgb(0,0,255);stroke-width:0" /><polygon points="34.890226,94.125000 33.890226,97.125000 34.890226,98.125000 35.890226,97.125000" style="fill:rgb(0,0,255);stroke:rgb(0,0,255);stroke-width:0" /> \n  <text x="32.890226" y="148.500000" font-family="inherit" font-size="3.6" fill="rgb(0,0,255)" text-anchor="middle" transform="rotate(-90.000000 32.890226,148.500000)" >435</text> </g>
  Visible = false
  X = 0
  Y = 0
  arrowL1 = 3
  arrowL2 = 1
  arrowW = 2
  arrow_scheme = 0
  autoPlaceOffset = 2
  autoPlaceText = true
  click1_x = 34.8902
  click1_y = 198.098
  click2_x = 34.8902
  click2_y = 198.098
  comma_decimal_place = false
  dimension_line_overshoot = 1
  gap_datum_points = 2
  halfDimension_linear = false
  lineColor = rgb(0,0,255)
  strokeWidth = 0.5
  textFormat_linear = %(value)3.3f
  textRenderer_color = rgb(0,0,255)
  textRenderer_family = inherit
  textRenderer_size = 3.6
  unit_custom_scale = 1
  unit_scheme = 0
FEATURE [Drawing::FeatureViewPython] dim012  # drawing view (typed FeaturePython)
  Rotation = 0
  ViewResult = <g> \n  <line x1="147.500000" y1="166.121850" x2="147.500000" y2="173.515226" style="stroke:rgb(0,0,255);stroke-width:0.50" />\n<line x1="122.500000" y1="166.121850" x2="122.500000" y2="173.515226" style="stroke:rgb(0,0,255);stroke-width:0.50" />\n<line x1="147.500000" y1="172.515226" x2="122.500000" y2="172.515226" style="stroke:rgb(0,0,255);stroke-width:0.50" /> \n  <polygon points="122.500000,172.515226 125.500000,173.515226 126.500000,172.515226 125.500000,171.515226" style="fill:rgb(0,0,255);stroke:rgb(0,0,255);stroke-width:0" /><polygon points="147.500000,172.515226 144.500000,171.515226 143.500000,172.515226 144.500000,173.515226" style="fill:rgb(0,0,255);stroke:rgb(0,0,255);stroke-width:0" /> \n  <text x="135.000000" y="170.515226" font-family="inherit" font-size="3.6" fill="rgb(0,0,255)" text-anchor="middle" transform="rotate(0.000000 135.000000,170.515226)" >100</text> </g>
  Visible = false
  X = 0
  Y = 0
  arrowL1 = 3
  arrowL2 = 1
  arrowW = 2
  arrow_scheme = 0
  autoPlaceOffset = 2
  autoPlaceText = true
  click1_x = 136.864
  click1_y = 172.515
  click2_x = 136.864
  click2_y = 172.515
  comma_decimal_place = false
  dimension_line_overshoot = 1
  gap_datum_points = 2
  halfDimension_linear = false
  lineColor = rgb(0,0,255)
  strokeWidth = 0.5
  textFormat_linear = %(value)3.3f
  textRenderer_color = rgb(0,0,255)
  textRenderer_family = inherit
  textRenderer_size = 3.6
  unit_custom_scale = 1
  unit_scheme = 0
FEATURE [Drawing::FeatureViewPython] centerLines006  # drawing view (typed FeaturePython)
  Rotation = 0
  ViewResult = <blob: 2232 chars omitted>
  Visible = false
  X = 0
  Y = 0
  centerLine_color = rgb(0,0,255)
  centerLine_len_dash = 6
  centerLine_len_dot = 1.5
  centerLine_len_gap = 2
  centerLine_width = 0.32
  click1_x = 126.895
  click1_y = 83.5285
  click2_x = 122.775
  click2_y = 83.6429
FEATURE [Drawing::FeatureViewPython] dim013  # drawing view (typed FeaturePython)
  Rotation = 0
  ViewResult = <g> \n  <line x1="62.500000" y1="87.513750" x2="62.500000" y2="79.453391" style="stroke:rgb(0,0,255);stroke-width:0.50" />\n<line x1="120.000000" y1="81.642921" x2="120.000000" y2="79.453391" style="stroke:rgb(0,0,255);stroke-width:0.50" />\n<line x1="62.500000" y1="80.453391" x2="120.000000" y2="80.453391" style="stroke:rgb(0,0,255);stroke-width:0.50" /> \n  <polygon points="120.000000,80.453391 117.000000,79.453391 116.000000,80.453391 117.000000,81.453391" style="fill:rgb(0,0,255);stroke:rgb(0,0,255);stroke-width:0" /><polygon points="62.500000,80.453391 65.500000,81.453391 66.500000,80.453391 65.500000,79.453391" style="fill:rgb(0,0,255);stroke:rgb(0,0,255);stroke-width:0" /> \n  <text x="91.250000" y="78.453391" font-family="inherit" font-size="3.6" fill="rgb(0,0,255)" text-anchor="middle" transform="rotate(0.000000 91.250000,78.453391)" >230</text> </g>
  Visible = false
  X = 0
  Y = 0
  arrowL1 = 3
  arrowL2 = 1
  arrowW = 2
  arrow_scheme = 0
  autoPlaceOffset = 2
  autoPlaceText = true
  click1_x = 118.131
  click1_y = 80.4534
  click2_x = 118.131
  click2_y = 80.4534
  comma_decimal_place = false
  dimension_line_overshoot = 1
  gap_datum_points = 2
  halfDimension_linear = false
  lineColor = rgb(0,0,255)
  strokeWidth = 0.5
  textFormat_linear = %(value)3.3f
  textRenderer_color = rgb(0,0,255)
  textRenderer_family = inherit
  textRenderer_size = 3.6
  unit_custom_scale = 1
  unit_scheme = 0
FEATURE [Drawing::FeatureViewPython] dim014  # drawing view (typed FeaturePython)
  Rotation = 0
  ViewResult = <g> \n  <line x1="147.500000" y1="87.271500" x2="147.500000" y2="79.344638" style="stroke:rgb(0,0,255);stroke-width:0.50" />\n<line x1="120.000000" y1="81.642921" x2="120.000000" y2="79.344638" style="stroke:rgb(0,0,255);stroke-width:0.50" />\n<line x1="147.500000" y1="80.344638" x2="120.000000" y2="80.344638" style="stroke:rgb(0,0,255);stroke-width:0.50" /> \n  <polygon points="120.000000,80.344638 123.000000,81.344638 124.000000,80.344638 123.000000,79.344638" style="fill:rgb(0,0,255);stroke:rgb(0,0,255);stroke-width:0" /><polygon points="147.500000,80.344638 144.500000,79.344638 143.500000,80.344638 144.500000,81.344638" style="fill:rgb(0,0,255);stroke:rgb(0,0,255);stroke-width:0" /> \n  <text x="133.750000" y="78.344638" font-family="inherit" font-size="3.6" fill="rgb(0,0,255)" text-anchor="middle" transform="rotate(0.000000 133.750000,78.344638)" >110</text> </g>
  Visible = false
  X = 0
  Y = 0
  arrowL1 = 3
  arrowL2 = 1
  arrowW = 2
  arrow_scheme = 0
  autoPlaceOffset = 2
  autoPlaceText = true
  click1_x = 124.925
  click1_y = 80.3446
  click2_x = 124.925
  click2_y = 80.3446
  comma_decimal_place = false
  dimension_line_overshoot = 1
  gap_datum_points = 2
  halfDimension_linear = false
  lineColor = rgb(0,0,255)
  strokeWidth = 0.5
  textFormat_linear = %(value)3.3f
  textRenderer_color = rgb(0,0,255)
  textRenderer_family = inherit
  textRenderer_size = 3.6
  unit_custom_scale = 1
  unit_scheme = 0
FEATURE [Drawing::FeatureViewPython] centerLines007  # drawing view (typed FeaturePython)
  Rotation = 0
  ViewResult = <g transform="scale(0.250000,0.250000)" stroke="rgb(0,0,255)"  stroke-width="1.280000" > <path d="M 590.000000,646.500000 L 584.000000,646.500000 M 576.000000,646.500000 L 552.000000,646.500000 M 544.000000,646.500000 L 538.000000,646.500000 M 530.000000,646.500000 L 506.000000,646.500000 M 498.000000,646.500000 L 492.000000,646.500000 M 484.000000,646.500000 L 460.000000,646.500000 M 452.000000,646.500000 L 446.000000,646.500000 M 438.000000,646.500000 L 436.386994,646.500000 "/>\n<path d="M 590.000000,646.500000 L 584.000000,646.500000 M 576.000000,646.500000 L 552.000000,646.500000 M 544.000000,646.500000 L 538.000000,646.500000 M 530.000000,646.500000 L 506.000000,646.500000 M 498.000000,646.500000 L 492.000000,646.500000 M 484.000000,646.500000 L 460.000000,646.500000 M 452.000000,646.500000 L 446.000000,646.500000 "/> </g> 
  Visible = false
  X = 0
  Y = 0
  centerLine_color = rgb(0,0,255)
  centerLine_len_dash = 6
  centerLine_len_dot = 1.5
  centerLine_len_gap = 2
  centerLine_width = 0.32
  click1_x = 109.097
  click1_y = 160.714
  click2_x = 110.515
  click2_y = 161.442
FEATURE [Drawing::FeatureViewPython] dim015  # drawing view (typed FeaturePython)
  Rotation = 0
  ViewResult = <g> \n  <line x1="124.496850" y1="202.875000" x2="161.279470" y2="202.875000" style="stroke:rgb(0,0,255);stroke-width:0.50" />\n<line x1="113.500000" y1="161.625000" x2="161.279470" y2="161.625000" style="stroke:rgb(0,0,255);stroke-width:0.50" />\n<line x1="160.279470" y1="202.875000" x2="160.279470" y2="161.625000" style="stroke:rgb(0,0,255);stroke-width:0.50" /> \n  <polygon points="160.279470,161.625000 159.279470,164.625000 160.279470,165.625000 161.279470,164.625000" style="fill:rgb(0,0,255);stroke:rgb(0,0,255);stroke-width:0" /><polygon points="160.279470,202.875000 161.279470,199.875000 160.279470,198.875000 159.279470,199.875000" style="fill:rgb(0,0,255);stroke:rgb(0,0,255);stroke-width:0" /> \n  <text x="158.279470" y="182.250000" font-family="inherit" font-size="3.6" fill="rgb(0,0,255)" text-anchor="middle" transform="rotate(-90.000000 158.279470,182.250000)" >165</text> </g>
  Visible = false
  X = 0
  Y = 0
  arrowL1 = 3
  arrowL2 = 1
  arrowW = 2
  arrow_scheme = 0
  autoPlaceOffset = 2
  autoPlaceText = true
  click1_x = 160.279
  click1_y = 179.051
  click2_x = 160.279
  click2_y = 179.051
  comma_decimal_place = false
  dimension_line_overshoot = 1
  gap_datum_points = 2
  halfDimension_linear = false
  lineColor = rgb(0,0,255)
  strokeWidth = 0.5
  textFormat_linear = %(value)3.3f
  textRenderer_color = rgb(0,0,255)
  textRenderer_family = inherit
  textRenderer_size = 3.6
  unit_custom_scale = 1
  unit_scheme = 0
FEATURE [Drawing::FeaturePage] Page001  label="BottomView"
  Group = -> [View002,View003,centerLines004,centerLines005,dim009,dim010,dim011,dim012,centerLines006,dim013,dim014,centerLines007,dim015]
  Template = <path>
note: 2 file-system paths scrubbed to <path> (originals preserved in the JSON sidecar)
